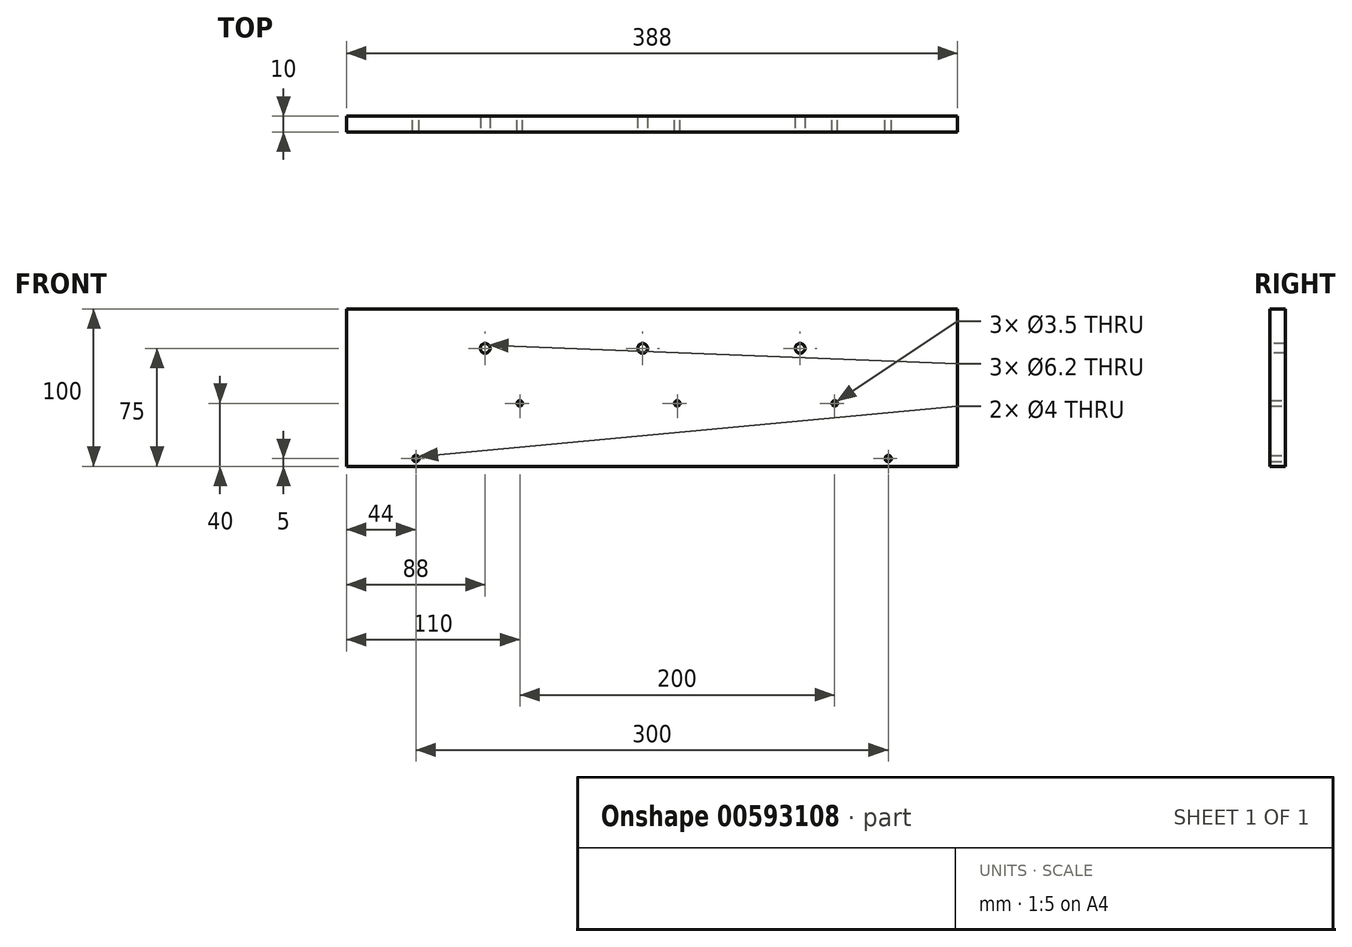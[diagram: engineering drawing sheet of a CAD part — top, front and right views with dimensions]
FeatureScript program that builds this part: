
annotation { "Feature Type Name" : "Feature", "Feature Type Description" : "" }
export const myFeature = defineFeature(function(context is Context, id is Id, definition is map)
    precondition{}
    {
        {
            var Q0;
            Q0=qCreatedBy(makeId("Front.planeOp"),FACE);
            var sketch = newSketch(context, id + "F0", { "sketchPlane" : qUnion([Q0])});
            skLineSegment(sketch, "E0.bottom", {"start": v(194, 50) * mm, "end": v(-194, 50) * mm});
            skLineSegment(sketch, "E0.top", {"start": v(194, -50) * mm, "end": v(-194, -50) * mm});
            skLineSegment(sketch, "E0.left", {"start": v(194, 50) * mm, "end": v(194, -50) * mm});
            skLineSegment(sketch, "E0.right", {"start": v(-194, 50) * mm, "end": v(-194, -50) * mm});
            skPoint(sketch, "E0.middle", {"position": v(0, 0) * mm});
            skCircle(sketch, "E1", {"center": v(150, -45) * mm, "radius": 2 * mm});
            skCircle(sketch, "E2", {"center": v(-150, -45) * mm, "radius": 2 * mm});
            skLineSegment(sketch, "E3", {"start": v(150, -45) * mm, "end": v(-150, -45) * mm, "construction": true});
            skPoint(sketch, "E4", {"position": v(0, -45) * mm});
            skCircle(sketch, "E5", {"center": v(116, -10) * mm, "radius": 1.75 * mm});
            skCircle(sketch, "E6", {"center": v(16, -10) * mm, "radius": 1.75 * mm});
            skCircle(sketch, "E7", {"center": v(-84, -10) * mm, "radius": 1.75 * mm});
            skLineSegment(sketch, "E8", {"start": v(-84, -10) * mm, "end": v(16, -10) * mm, "construction": true});
            skLineSegment(sketch, "E9", {"start": v(116, -10) * mm, "end": v(16, -10) * mm, "construction": true});
            skSolve(sketch);
        }
        {
            var Q0;
            Q0=qSketchRegion(id+"F0",true);
            extrude(context, id + "F1", {"entities" : qUnion([Q0]), "depth" : 10 * mm, "offsetDistance" : 25 * mm});
        }
        {
            var Q0;
            Q0=makeQuery(id+"F1.opExtrude","CAP_FACE",FACE,{"disambiguationData":[OSD([sQuery(id+"F0.wireOp",EDGE,"E0.bottom"),sQuery(id+"F0.wireOp",EDGE,"E0.top"),sQuery(id+"F0.wireOp",EDGE,"E0.left"),sQuery(id+"F0.wireOp",EDGE,"E0.right"),sQuery(id+"F0.wireOp",EDGE,"E1"),sQuery(id+"F0.wireOp",EDGE,"E2"),sQuery(id+"F0.wireOp",EDGE,"E5"),sQuery(id+"F0.wireOp",EDGE,"E6"),sQuery(id+"F0.wireOp",EDGE,"E7")])],"isStart":false});
            var sketch = newSketch(context, id + "F2", { "sketchPlane" : qUnion([Q0])});
            skCircle(sketch, "E10", {"center": v(-6, 25) * mm, "radius": 3.1 * mm});
            skCircle(sketch, "E11", {"center": v(94, 25) * mm, "radius": 3.1 * mm});
            skCircle(sketch, "E12", {"center": v(-106, 25) * mm, "radius": 3.1 * mm});
            skSolve(sketch);
        }
        {
            var Q0;
            Q0=qSketchRegion(id+"F2",true);
            extrude(context, id + "F3", {"entities" : qUnion([Q0]), "operationType" : NewBodyOperationType.REMOVE, "oppositeDirection" : true, "depth" : 25 * mm, "offsetDistance" : 25 * mm});
        }
    });
